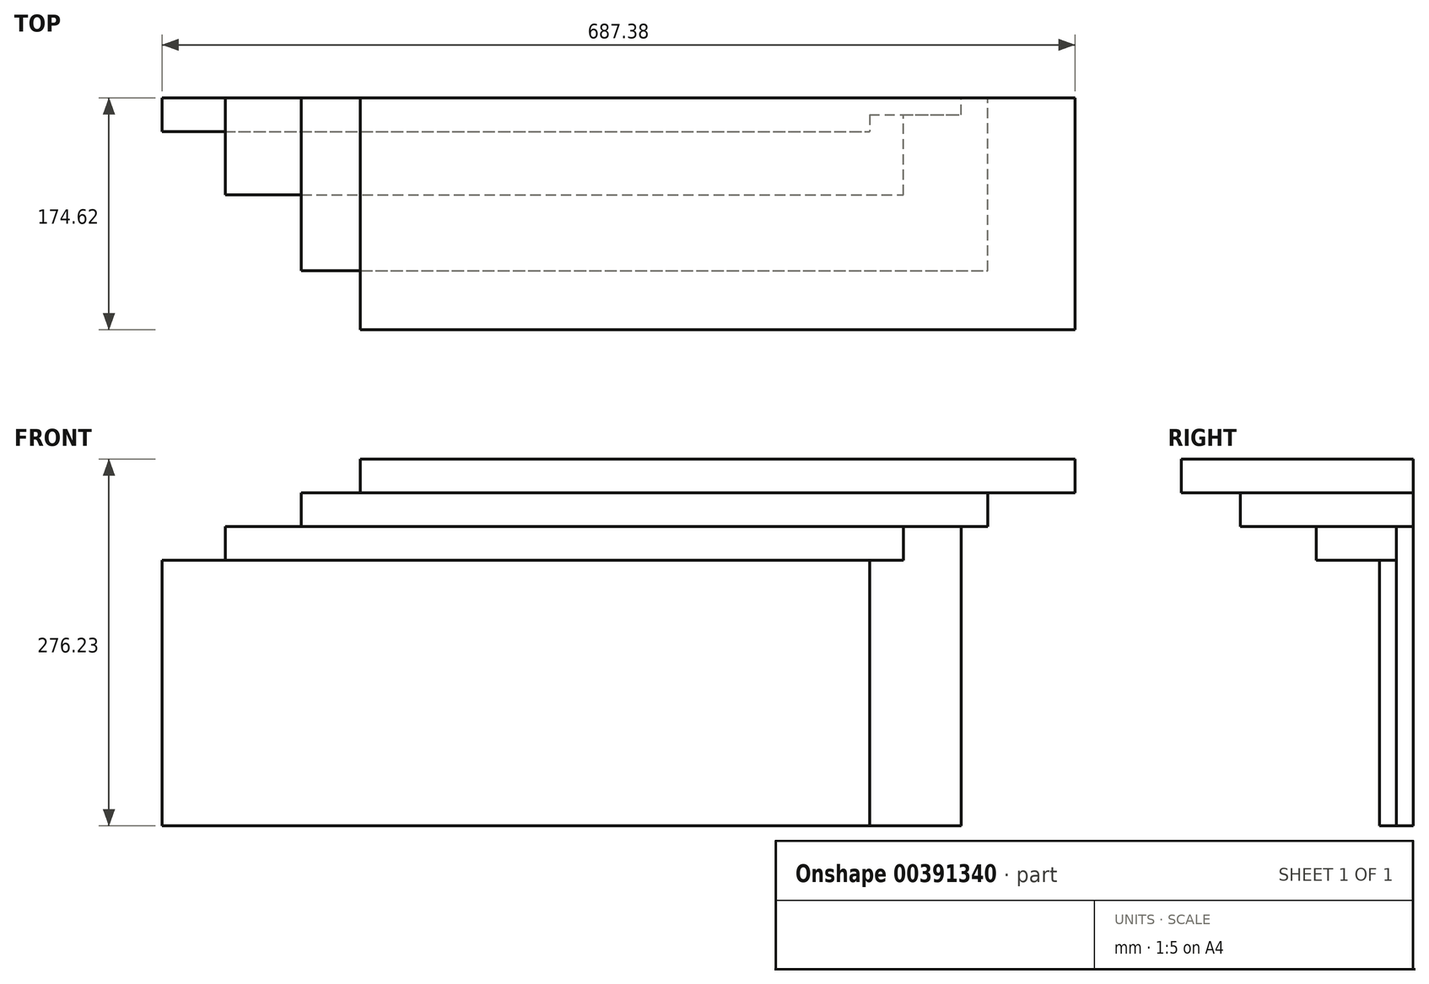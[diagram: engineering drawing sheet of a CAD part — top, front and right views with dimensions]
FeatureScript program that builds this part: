
annotation { "Feature Type Name" : "Feature", "Feature Type Description" : "" }
export const myFeature = defineFeature(function(context is Context, id is Id, definition is map)
    precondition{}
    {
        {
            var Q0;
            Q0=qCreatedBy(makeId("Front.planeOp"),FACE);
            var sketch = newSketch(context, id + "F0", { "sketchPlane" : qUnion([Q0])});
            skLineSegment(sketch, "E0.bottom", {"start": v(-775.5, 0) * mm, "end": v(775.5, 0) * mm});
            skLineSegment(sketch, "E0.top", {"start": v(-775.5, -25.4) * mm, "end": v(775.5, -25.4) * mm});
            skLineSegment(sketch, "E0.left", {"start": v(-775.5, 0) * mm, "end": v(-775.5, -25.4) * mm});
            skLineSegment(sketch, "E0.right", {"start": v(775.5, 0) * mm, "end": v(775.5, -25.4) * mm});
            skSolve(sketch);
        }
        {
            var Q0;
            Q0=qSketchRegion(id+"F0",true);
            extrude(context, id + "F1", {"entities" : qUnion([Q0]), "depth" : 174.62 * mm});
        }
        {
            var Q0;
            Q0=qCreatedBy(makeId("Front.planeOp"),FACE);
            var sketch = newSketch(context, id + "F2", { "sketchPlane" : qUnion([Q0])});
            skLineSegment(sketch, "E1.bottom", {"start": v(-673.9, -25.4) * mm, "end": v(689.77, -25.4) * mm});
            skLineSegment(sketch, "E1.top", {"start": v(-673.9, -276.23) * mm, "end": v(689.77, -276.23) * mm});
            skLineSegment(sketch, "E1.left", {"start": v(-673.9, -25.4) * mm, "end": v(-673.9, -276.22) * mm});
            skLineSegment(sketch, "E1.right", {"start": v(689.77, -25.4) * mm, "end": v(689.77, -276.23) * mm});
            skSolve(sketch);
        }
        {
            var Q0;
            Q0=qCreatedBy(makeId("Front.planeOp"),FACE);
            var sketch = newSketch(context, id + "F3", { "sketchPlane" : qUnion([Q0])});
            skLineSegment(sketch, "E2.bottom", {"start": v(-709.61, -25.4) * mm, "end": v(709.61, -25.4) * mm});
            skLineSegment(sketch, "E2.top", {"start": v(-709.61, -50.8) * mm, "end": v(709.61, -50.8) * mm});
            skLineSegment(sketch, "E2.left", {"start": v(-709.61, -25.4) * mm, "end": v(-709.61, -50.8) * mm});
            skLineSegment(sketch, "E2.right", {"start": v(709.61, -25.4) * mm, "end": v(709.61, -50.8) * mm});
            skSolve(sketch);
        }
        {
            var Q0;
            Q0=qSketchRegion(id+"F3",true);
            extrude(context, id + "F4", {"entities" : qUnion([Q0]), "operationType" : NewBodyOperationType.ADD, "depth" : 130.17 * mm});
        }
        {
            var Q0;
            Q0=qCreatedBy(makeId("Front.planeOp"),FACE);
            var sketch = newSketch(context, id + "F5", { "sketchPlane" : qUnion([Q0])});
            skLineSegment(sketch, "E3.bottom", {"start": v(-646.11, -50.8) * mm, "end": v(646.11, -50.8) * mm});
            skLineSegment(sketch, "E3.top", {"start": v(-646.11, -76.2) * mm, "end": v(646.11, -76.2) * mm});
            skLineSegment(sketch, "E3.left", {"start": v(-646.11, -50.8) * mm, "end": v(-646.11, -76.2) * mm});
            skLineSegment(sketch, "E3.right", {"start": v(646.11, -50.8) * mm, "end": v(646.11, -76.2) * mm});
            skSolve(sketch);
        }
        {
            var Q0;
            Q0=qSketchRegion(id+"F5",true);
            extrude(context, id + "F6", {"entities" : qUnion([Q0]), "operationType" : NewBodyOperationType.ADD, "depth" : 73.02 * mm});
        }
        {
            var Q0;
            Q0=makeQuery(id+"F2.imprint","IMPRINT",FACE,{"disambiguationData":[TD([[makeQuery(id+"F2.imprint","IMPRINT",EDGE,{"derivedFrom":sQuery(id+"F2.wireOp",EDGE,"E1.bottom")}),-1.0]])]});
            extrude(context, id + "F7", {"entities" : qUnion([Q0]), "operationType" : NewBodyOperationType.ADD, "depth" : 25.4 * mm});
        }
        {
            var Q0;
            Q0=makeQuery(id+"F7.opExtrude","CAP_FACE",FACE,{"disambiguationData":[OSD([sQuery(id+"F2.wireOp",EDGE,"E1.bottom"),sQuery(id+"F2.wireOp",EDGE,"E1.top"),sQuery(id+"F2.wireOp",EDGE,"E1.left"),sQuery(id+"F2.wireOp",EDGE,"E1.right")])],"isStart":false});
            var sketch = newSketch(context, id + "F8", { "sketchPlane" : qUnion([Q0])});
            skLineSegment(sketch, "E4.bottom", {"start": v(-673.9, -276.22) * mm, "end": v(-620.71, -276.22) * mm});
            skLineSegment(sketch, "E4.top", {"start": v(-673.9, -50.8) * mm, "end": v(-620.71, -50.8) * mm});
            skLineSegment(sketch, "E4.left", {"start": v(-673.9, -276.22) * mm, "end": v(-673.9, -50.8) * mm});
            skLineSegment(sketch, "E4.right", {"start": v(-620.71, -276.22) * mm, "end": v(-620.71, -50.8) * mm});
            skLineSegment(sketch, "E5.bottom", {"start": v(689.77, -276.23) * mm, "end": v(620.71, -276.23) * mm});
            skLineSegment(sketch, "E5.top", {"start": v(689.77, -50.8) * mm, "end": v(620.71, -50.8) * mm});
            skLineSegment(sketch, "E5.left", {"start": v(689.77, -276.23) * mm, "end": v(689.77, -50.8) * mm});
            skLineSegment(sketch, "E5.right", {"start": v(620.71, -276.22) * mm, "end": v(620.71, -50.8) * mm});
            skSolve(sketch);
        }
        {
            var Q0;
            {var subQ1=sQuery(id+"F8.wireOp",EDGE,"E4.bottom");Q0=makeQuery(id+"F8.imprint","IMPRINT",FACE,{"disambiguationData":[TD([[makeQuery(id+"F8.imprint","IMPRINT",EDGE,{"derivedFrom":subQ1}),1.0]])]});}
            var Q1;
            {var subQ1=sQuery(id+"F8.wireOp",EDGE,"E5.bottom");Q1=makeQuery(id+"F8.imprint","IMPRINT",FACE,{"disambiguationData":[TD([[makeQuery(id+"F8.imprint","IMPRINT",EDGE,{"derivedFrom":subQ1}),1.0]])]});}
            extrude(context, id + "F9", {"entities" : qUnion([Q0, Q1]), "operationType" : NewBodyOperationType.REMOVE, "oppositeDirection" : true, "depth" : 12.7 * mm});
        }
        {
            var Q0;
            Q0=qCreatedBy(makeId("Front.planeOp"),FACE);
            var sketch = newSketch(context, id + "F10", { "sketchPlane" : qUnion([Q0])});
            skLineSegment(sketch, "E6.bottom", {"start": v(88.1, 146.12) * mm, "end": v(-848.8, 146.12) * mm});
            skLineSegment(sketch, "E6.top", {"start": v(88.1, -385.73) * mm, "end": v(-848.8, -385.73) * mm});
            skLineSegment(sketch, "E6.left", {"start": v(88.1, 146.12) * mm, "end": v(88.1, -385.73) * mm});
            skLineSegment(sketch, "E6.right", {"start": v(-848.8, 146.12) * mm, "end": v(-848.8, -385.73) * mm});
            skSolve(sketch);
        }
        {
            var Q0;
            Q0=makeQuery(id+"F10.imprint","IMPRINT",FACE,{"disambiguationData":[TD([[makeQuery(id+"F10.imprint","IMPRINT",EDGE,{"derivedFrom":sQuery(id+"F10.wireOp",EDGE,"E6.bottom")}),1.0]])]});
            extrude(context, id + "F11", {"entities" : qUnion([Q0]), "operationType" : NewBodyOperationType.REMOVE, "endBound" : BoundingType.THROUGH_ALL, "depth" : 25.4 * mm});
        }
        {
            var Q0;
            Q0=qCreatedBy(makeId("Front.planeOp"),FACE);
            var sketch = newSketch(context, id + "F12", { "sketchPlane" : qUnion([Q0])});
            skLineSegment(sketch, "E7", {"start": v(237.33, 0) * mm, "end": v(237.33, -25.4) * mm});
            skLineSegment(sketch, "E8", {"start": v(237.33, -25.4) * mm, "end": v(192.88, -25.4) * mm});
            skLineSegment(sketch, "E9", {"start": v(192.88, -25.4) * mm, "end": v(192.88, -50.8) * mm});
            skLineSegment(sketch, "E10", {"start": v(192.88, -50.8) * mm, "end": v(135.73, -50.8) * mm});
            skLineSegment(sketch, "E11", {"start": v(135.73, -50.8) * mm, "end": v(135.73, -76.2) * mm});
            skLineSegment(sketch, "E12", {"start": v(135.73, -76.2) * mm, "end": v(88.1, -76.2) * mm});
            skLineSegment(sketch, "E13", {"start": v(237.33, 0) * mm, "end": v(148.37, 68.83) * mm});
            skLineSegment(sketch, "E14", {"start": v(148.37, 68.83) * mm, "end": v(-112.54, 31.02) * mm});
            skLineSegment(sketch, "E15", {"start": v(-112.54, 31.02) * mm, "end": v(38.71, -95.66) * mm});
            skLineSegment(sketch, "E16", {"start": v(38.71, -95.66) * mm, "end": v(88.1, -76.2) * mm});
            skSolve(sketch);
        }
        {
            var Q0;
            Q0=makeQuery(id+"F12.imprint","IMPRINT",FACE,{"disambiguationData":[TD([[makeQuery(id+"F12.imprint","IMPRINT",EDGE,{"derivedFrom":sQuery(id+"F12.wireOp",EDGE,"E7")}),-1.0]])]});
            extrude(context, id + "F13", {"entities" : qUnion([Q0]), "operationType" : NewBodyOperationType.REMOVE, "endBound" : BoundingType.THROUGH_ALL, "depth" : 25.4 * mm});
        }
    });
